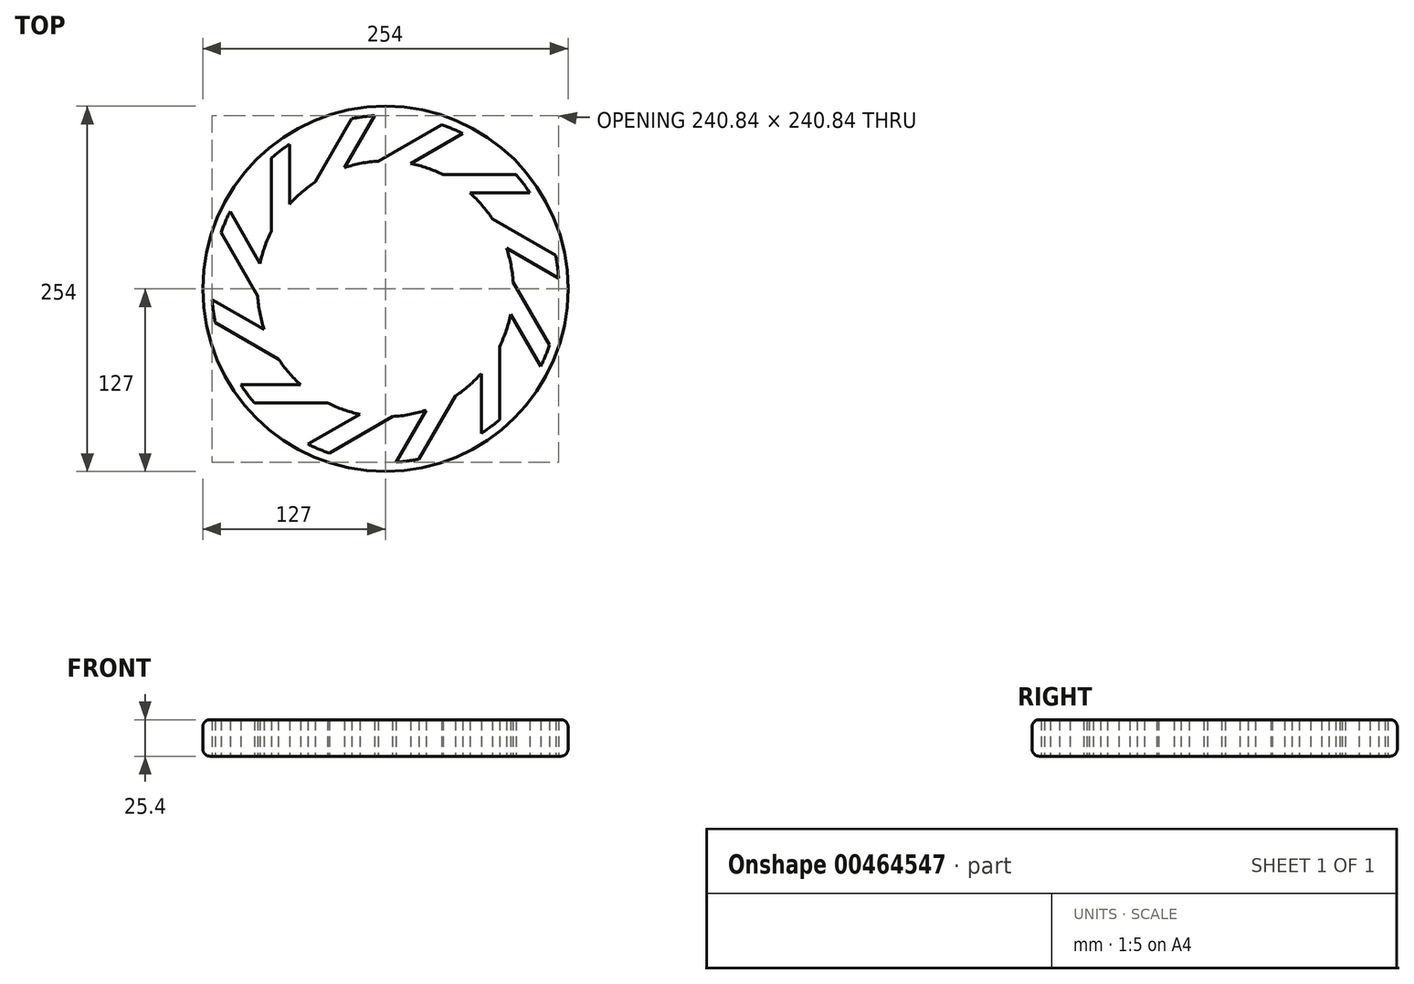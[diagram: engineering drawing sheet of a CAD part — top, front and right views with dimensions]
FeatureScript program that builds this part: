
annotation { "Feature Type Name" : "Feature", "Feature Type Description" : "" }
export const myFeature = defineFeature(function(context is Context, id is Id, definition is map)
    precondition{}
    {
        {
            var Q0;
            Q0=qCreatedBy(makeId("Top.planeOp"),FACE);
            var sketch = newSketch(context, id + "F0", { "sketchPlane" : qUnion([Q0])});
            skCircle(sketch, "E0", {"center": v(0, 0) * mm, "radius": 120.65 * mm});
            skCircle(sketch, "E1", {"center": v(0, 0) * mm, "radius": 88.9 * mm});
            skLineSegment(sketch, "E2", {"start": v(-79.35, 40.08) * mm, "end": v(-79.35, 90.88) * mm});
            skLineSegment(sketch, "E3", {"start": v(-66.65, 58.83) * mm, "end": v(-66.65, 100.57) * mm});
            skLineSegment(sketch, "E4", {"start": v(-48.68, 74.39) * mm, "end": v(-23.28, 118.38) * mm});
            skLineSegment(sketch, "E5", {"start": v(-28.3, 84.27) * mm, "end": v(-7.44, 120.42) * mm});
            skLineSegment(sketch, "E6", {"start": v(-4.96, 88.76) * mm, "end": v(39.03, 114.16) * mm});
            skLineSegment(sketch, "E7", {"start": v(17.62, 87.14) * mm, "end": v(53.77, 108) * mm});
            skLineSegment(sketch, "E8", {"start": v(40.08, 79.35) * mm, "end": v(90.88, 79.35) * mm});
            skLineSegment(sketch, "E9", {"start": v(58.83, 66.65) * mm, "end": v(100.57, 66.65) * mm});
            skLineSegment(sketch, "E10", {"start": v(74.39, 48.68) * mm, "end": v(118.38, 23.28) * mm});
            skLineSegment(sketch, "E11", {"start": v(84.27, 28.3) * mm, "end": v(120.42, 7.44) * mm});
            skLineSegment(sketch, "E12", {"start": v(88.76, 4.96) * mm, "end": v(114.16, -39.03) * mm});
            skLineSegment(sketch, "E13", {"start": v(87.14, -17.62) * mm, "end": v(108, -53.77) * mm});
            skLineSegment(sketch, "E14", {"start": v(79.35, -40.08) * mm, "end": v(79.35, -90.88) * mm});
            skLineSegment(sketch, "E15", {"start": v(66.65, -58.83) * mm, "end": v(66.65, -100.57) * mm});
            skLineSegment(sketch, "E16", {"start": v(48.68, -74.39) * mm, "end": v(23.28, -118.38) * mm});
            skLineSegment(sketch, "E17", {"start": v(28.3, -84.27) * mm, "end": v(7.44, -120.42) * mm});
            skLineSegment(sketch, "E18", {"start": v(4.96, -88.76) * mm, "end": v(-39.03, -114.16) * mm});
            skLineSegment(sketch, "E19", {"start": v(-17.62, -87.14) * mm, "end": v(-53.77, -108) * mm});
            skLineSegment(sketch, "E20", {"start": v(-40.08, -79.35) * mm, "end": v(-90.88, -79.35) * mm});
            skLineSegment(sketch, "E21", {"start": v(-58.83, -66.65) * mm, "end": v(-100.57, -66.65) * mm});
            skLineSegment(sketch, "E22", {"start": v(-74.39, -48.68) * mm, "end": v(-118.38, -23.28) * mm});
            skLineSegment(sketch, "E23", {"start": v(-84.27, -28.3) * mm, "end": v(-120.42, -7.44) * mm});
            skLineSegment(sketch, "E24", {"start": v(-88.76, -4.96) * mm, "end": v(-114.16, 39.03) * mm});
            skLineSegment(sketch, "E25", {"start": v(-87.14, 17.62) * mm, "end": v(-108, 53.77) * mm});
            skCircle(sketch, "E26", {"center": v(0, 0) * mm, "radius": 127 * mm});
            skSolve(sketch);
        }
        {
            var Q0;
            Q0 = qSketchRegion(id + "F0", true);
            var Q1;
            {var subQ0=sQuery(id+"F0.wireOp",EDGE,"E2");Q1=makeQuery(id+"F0.imprint","IMPRINT",FACE,{"disambiguationData":[TD([[makeQuery(id+"F0.imprint","IMPRINT",EDGE,{"derivedFrom":subQ0}),1.0]])]});}
            var Q2;
            {var subQ0=sQuery(id+"F0.wireOp",EDGE,"E3");Q2=makeQuery(id+"F0.imprint","IMPRINT",FACE,{"disambiguationData":[TD([[makeQuery(id+"F0.imprint","IMPRINT",EDGE,{"derivedFrom":subQ0}),-1.0]])]});}
            var Q3;
            {var subQ0=sQuery(id+"F0.wireOp",EDGE,"E5");Q3=makeQuery(id+"F0.imprint","IMPRINT",FACE,{"disambiguationData":[TD([[makeQuery(id+"F0.imprint","IMPRINT",EDGE,{"derivedFrom":subQ0}),-1.0]])]});}
            var Q4;
            {var subQ0=sQuery(id+"F0.wireOp",EDGE,"E7");Q4=makeQuery(id+"F0.imprint","IMPRINT",FACE,{"disambiguationData":[TD([[makeQuery(id+"F0.imprint","IMPRINT",EDGE,{"derivedFrom":subQ0}),-1.0]])]});}
            var Q5;
            {var subQ0=sQuery(id+"F0.wireOp",EDGE,"E9");Q5=makeQuery(id+"F0.imprint","IMPRINT",FACE,{"disambiguationData":[TD([[makeQuery(id+"F0.imprint","IMPRINT",EDGE,{"derivedFrom":subQ0}),-1.0]])]});}
            var Q6;
            {var subQ0=sQuery(id+"F0.wireOp",EDGE,"E11");Q6=makeQuery(id+"F0.imprint","IMPRINT",FACE,{"disambiguationData":[TD([[makeQuery(id+"F0.imprint","IMPRINT",EDGE,{"derivedFrom":subQ0}),-1.0]])]});}
            var Q7;
            {var subQ0=sQuery(id+"F0.wireOp",EDGE,"E13");Q7=makeQuery(id+"F0.imprint","IMPRINT",FACE,{"disambiguationData":[TD([[makeQuery(id+"F0.imprint","IMPRINT",EDGE,{"derivedFrom":subQ0}),-1.0]])]});}
            var Q8;
            {var subQ0=sQuery(id+"F0.wireOp",EDGE,"E15");Q8=makeQuery(id+"F0.imprint","IMPRINT",FACE,{"disambiguationData":[TD([[makeQuery(id+"F0.imprint","IMPRINT",EDGE,{"derivedFrom":subQ0}),-1.0]])]});}
            var Q9;
            {var subQ0=sQuery(id+"F0.wireOp",EDGE,"E19");Q9=makeQuery(id+"F0.imprint","IMPRINT",FACE,{"disambiguationData":[TD([[makeQuery(id+"F0.imprint","IMPRINT",EDGE,{"derivedFrom":subQ0}),-1.0]])]});}
            var Q10;
            {var subQ0=sQuery(id+"F0.wireOp",EDGE,"E17");Q10=makeQuery(id+"F0.imprint","IMPRINT",FACE,{"disambiguationData":[TD([[makeQuery(id+"F0.imprint","IMPRINT",EDGE,{"derivedFrom":subQ0}),-1.0]])]});}
            var Q11;
            {var subQ0=sQuery(id+"F0.wireOp",EDGE,"E21");Q11=makeQuery(id+"F0.imprint","IMPRINT",FACE,{"disambiguationData":[TD([[makeQuery(id+"F0.imprint","IMPRINT",EDGE,{"derivedFrom":subQ0}),-1.0]])]});}
            var Q12;
            {var subQ0=sQuery(id+"F0.wireOp",EDGE,"E23");Q12=makeQuery(id+"F0.imprint","IMPRINT",FACE,{"disambiguationData":[TD([[makeQuery(id+"F0.imprint","IMPRINT",EDGE,{"derivedFrom":subQ0}),-1.0]])]});}
            extrude(context, id + "F1", {"entities" : qUnion([Q0, Q1, Q2, Q3, Q4, Q5, Q6, Q7, Q8, Q9, Q10, Q11, Q12]), "depth" : 25.4 * mm});
        }
        {
            var Q0;
            Q0=makeQuery(id+"F1.opExtrude","CAP_EDGE",EDGE,{"disambiguationData":[OSD([sQuery(id+"F0.wireOp",EDGE,"E26")])],"isStart":false});
            var Q1;
            Q1=makeQuery(id+"F1.opExtrude","CAP_EDGE",EDGE,{"disambiguationData":[OSD([sQuery(id+"F0.wireOp",EDGE,"E26")])],"isStart":true});
            fillet(context, id + "F2", {"entities" : qUnion([Q0, Q1]), "radius" : 5.08 * mm, "tangentPropagation" : true, "allowEdgeOverflow" : false});
        }
    });
